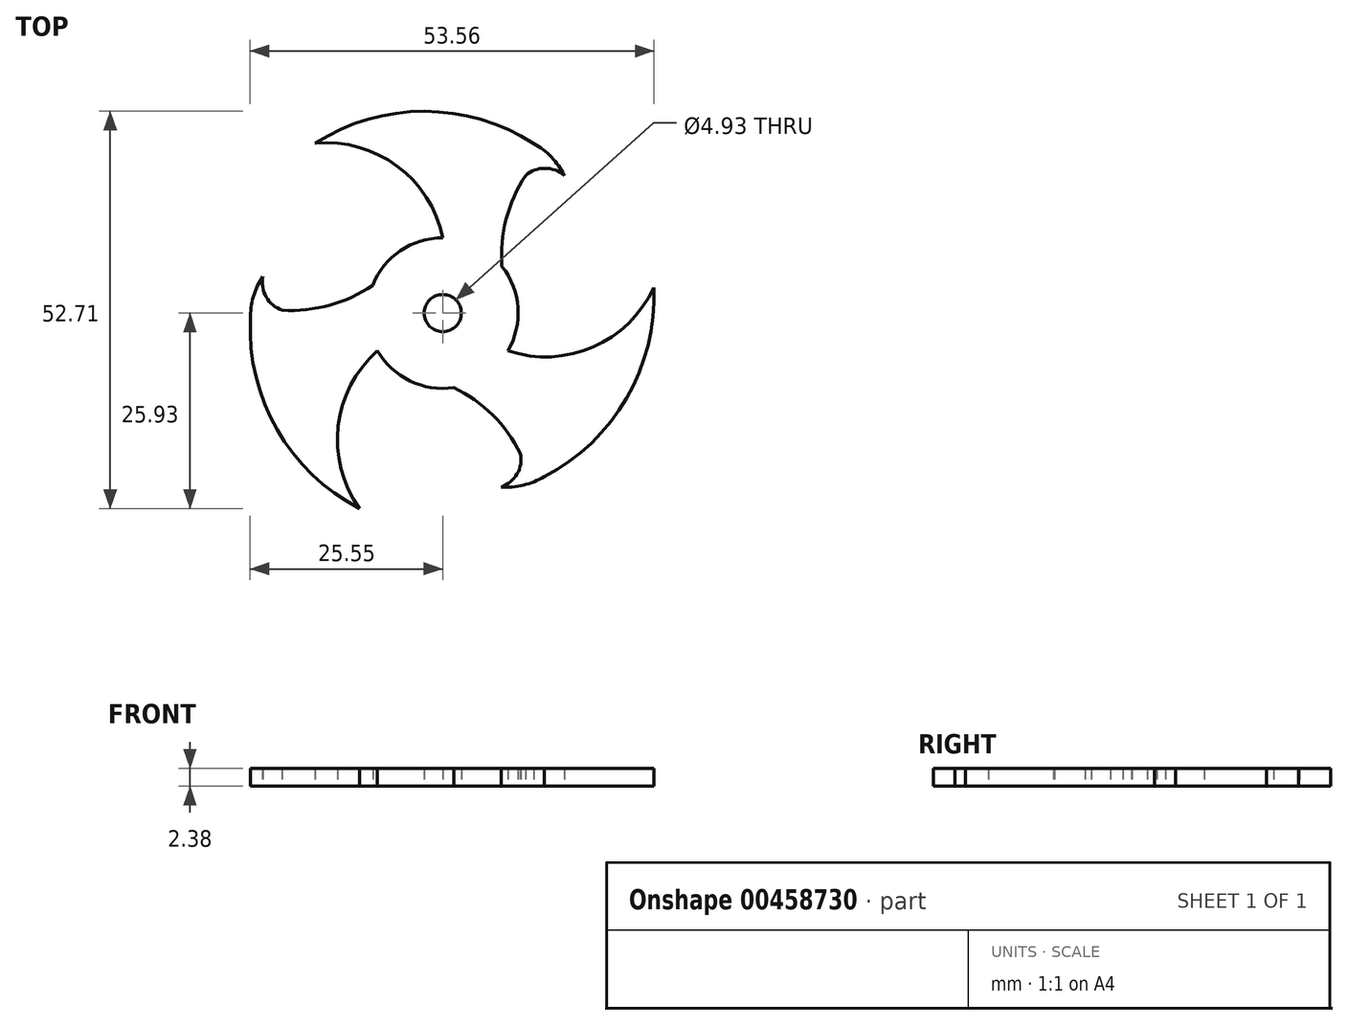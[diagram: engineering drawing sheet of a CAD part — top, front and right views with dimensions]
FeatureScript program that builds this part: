
annotation { "Feature Type Name" : "Feature", "Feature Type Description" : "" }
export const myFeature = defineFeature(function(context is Context, id is Id, definition is map)
    precondition{}
    {
        {
            var Q0;
            Q0=qCreatedBy(makeId("Top.planeOp"),FACE);
            var sketch = newSketch(context, id + "F0", { "sketchPlane" : qUnion([Q0])});
            skCircle(sketch, "E0", {"center": v(0, 0) * mm, "radius": 10 * mm});
            skCircle(sketch, "E1", {"center": v(0, 0) * mm, "radius": 2.46 * mm});
            skArc(sketch, "E2", {"start": v(0, 10) * mm, "mid": v(-6.06, 19.52) * mm, "end": v(-16.93, 22.54) * mm});
            skArc(sketch, "E3", {"start": v(12.07, 22.5) * mm, "mid": v(-2.42, 26.78) * mm, "end": v(-16.93, 22.54) * mm});
            skArc(sketch, "E4", {"start": v(16.12, 18.25) * mm, "mid": v(14.43, 20.7) * mm, "end": v(12.07, 22.5) * mm});
            skArc(sketch, "E5", {"start": v(16.12, 18.25) * mm, "mid": v(13.55, 19.22) * mm, "end": v(10.98, 18.25) * mm});
            skArc(sketch, "E6", {"start": v(10.98, 18.25) * mm, "mid": v(8.41, 12.49) * mm, "end": v(7.85, 6.2) * mm});
            skArc(sketch, "E7.1.0", {"start": v(-8.66, -5) * mm, "mid": v(-13.87, -15) * mm, "end": v(-11.06, -25.93) * mm});
            skArc(sketch, "E7.1.1", {"start": v(-25.51, -0.8) * mm, "mid": v(-21.98, -15.49) * mm, "end": v(-11.06, -25.93) * mm});
            skArc(sketch, "E7.1.2", {"start": v(-23.87, 4.84) * mm, "mid": v(-25.14, 2.15) * mm, "end": v(-25.51, -0.8) * mm});
            skArc(sketch, "E7.1.3", {"start": v(-23.87, 4.84) * mm, "mid": v(-23.42, 2.13) * mm, "end": v(-21.3, 0.39) * mm});
            skArc(sketch, "E7.1.4", {"start": v(-21.3, 0.39) * mm, "mid": v(-15.02, 1.04) * mm, "end": v(-9.3, 3.7) * mm});
            skArc(sketch, "E7.2.0", {"start": v(8.66, -5) * mm, "mid": v(19.93, -4.51) * mm, "end": v(27.98, 3.39) * mm});
            skArc(sketch, "E7.2.1", {"start": v(13.45, -21.7) * mm, "mid": v(24.4, -11.3) * mm, "end": v(27.98, 3.39) * mm});
            skArc(sketch, "E7.2.2", {"start": v(7.75, -23.1) * mm, "mid": v(10.7, -22.85) * mm, "end": v(13.45, -21.7) * mm});
            skArc(sketch, "E7.2.3", {"start": v(7.75, -23.1) * mm, "mid": v(9.87, -21.35) * mm, "end": v(10.31, -18.64) * mm});
            skArc(sketch, "E7.2.4", {"start": v(10.31, -18.64) * mm, "mid": v(6.6, -13.53) * mm, "end": v(1.44, -9.9) * mm});
            skSolve(sketch);
        }
        {
            var Q0;
            {var subQ0=sQuery(id+"F0.wireOp",EDGE,"E2");Q0=makeQuery(id+"F0.imprint","IMPRINT",FACE,{"disambiguationData":[TD([[makeQuery(id+"F0.imprint","IMPRINT",EDGE,{"derivedFrom":subQ0}),-1.0]])]});}
            var Q1;
            {var subQ0=sQuery(id+"F0.wireOp",EDGE,"E7.1.0");Q1=makeQuery(id+"F0.imprint","IMPRINT",FACE,{"disambiguationData":[TD([[makeQuery(id+"F0.imprint","IMPRINT",EDGE,{"derivedFrom":subQ0}),-1.0]])]});}
            var Q2;
            {var subQ0=sQuery(id+"F0.wireOp",EDGE,"E7.2.0");Q2=makeQuery(id+"F0.imprint","IMPRINT",FACE,{"disambiguationData":[TD([[makeQuery(id+"F0.imprint","IMPRINT",EDGE,{"derivedFrom":subQ0}),-1.0]])]});}
            var Q3;
            Q3=makeQuery(id+"F0.imprint","IMPRINT",FACE,{"disambiguationData":[TD([[makeQuery(id+"F0.imprint","IMPRINT",EDGE,{"derivedFrom":sQuery(id+"F0.wireOp",EDGE,"E1")}),-1.0]])]});
            extrude(context, id + "F1", {"entities" : qUnion([Q0, Q1, Q2, Q3]), "depth" : 2.38 * mm, "offsetDistance" : 25 * mm});
        }
    });
